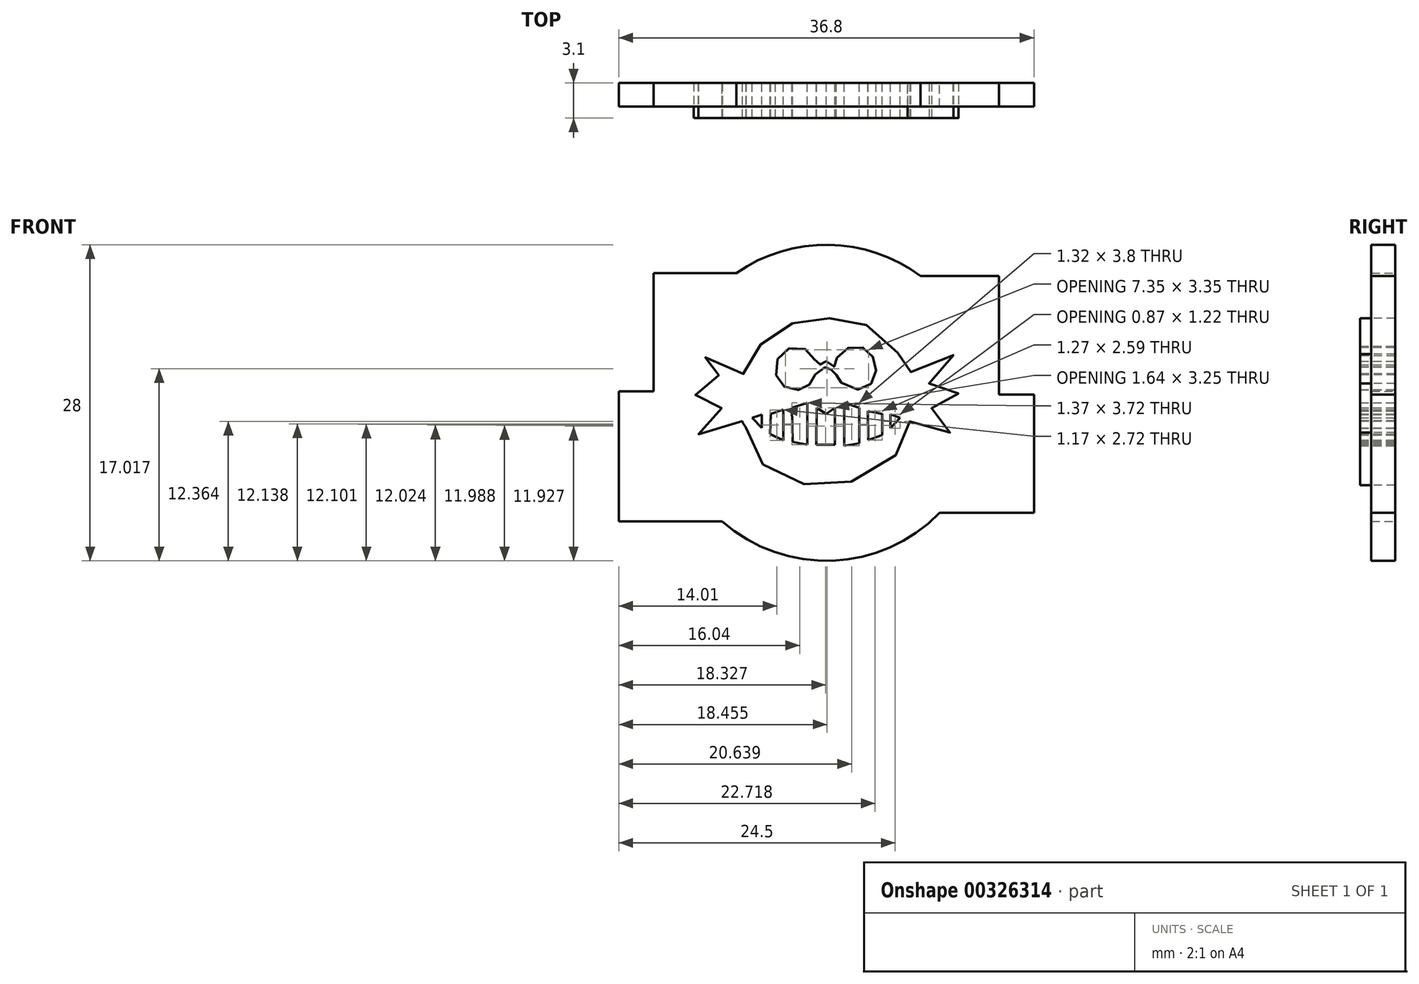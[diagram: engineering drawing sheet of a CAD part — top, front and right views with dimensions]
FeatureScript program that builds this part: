
annotation { "Feature Type Name" : "Feature", "Feature Type Description" : "" }
export const myFeature = defineFeature(function(context is Context, id is Id, definition is map)
    precondition{}
    {
        {
            var Q0;
            Q0=qCreatedBy(makeId("Front.planeOp"),FACE);
            var sketch = newSketch(context, id + "F0", { "sketchPlane" : qUnion([Q0])});
            skArc(sketch, "E0", {"start": v(-9.26, -10.5) * mm, "mid": v(-4.95, -13.1) * mm, "end": v(0, -14) * mm});
            skLineSegment(sketch, "E1", {"start": v(0, 0) * mm, "end": v(0, -32.67) * mm});
            skLineSegment(sketch, "E2", {"start": v(0, -32.67) * mm, "end": v(0, 0) * mm});
            skLineSegment(sketch, "E3", {"start": v(0, 0) * mm, "end": v(0, 29.65) * mm});
            skLineSegment(sketch, "E4", {"start": v(0, 29.65) * mm, "end": v(0, 0) * mm});
            skLineSegment(sketch, "E5", {"start": v(-26.07, 0) * mm, "end": v(57.02, 0) * mm});
            skLineSegment(sketch, "E6", {"start": v(-18.4, 1) * mm, "end": v(-15.3, 1) * mm});
            skLineSegment(sketch, "E7", {"start": v(-15.3, 1) * mm, "end": v(-15.3, 11.5) * mm});
            skLineSegment(sketch, "E8", {"start": v(-15.3, 11.5) * mm, "end": v(-7.97, 11.5) * mm});
            skLineSegment(sketch, "E9", {"start": v(-18.4, -10.5) * mm, "end": v(-9.26, -10.5) * mm});
            skPoint(sketch, "E10.start.orphan", {"position": v(-26.07, 0) * mm});
            skLineSegment(sketch, "E11", {"start": v(-18.4, 1) * mm, "end": v(-18.4, -10.5) * mm});
            skArc(sketch, "E12.trimOffspring", {"start": v(0, 14) * mm, "mid": v(-4.18, 13.36) * mm, "end": v(-7.97, 11.5) * mm});
            skSolve(sketch);
        }
        {
            var Q0;
            Q0=qCreatedBy(makeId("Front.planeOp"),FACE);
            var sketch = newSketch(context, id + "F1", { "sketchPlane" : qUnion([Q0])});
            skLineSegment(sketch, "E13", {"start": v(18.4, -9.75) * mm, "end": v(18.4, 0.75) * mm});
            skLineSegment(sketch, "E14", {"start": v(18.4, 0.75) * mm, "end": v(15.3, 0.75) * mm});
            skLineSegment(sketch, "E15", {"start": v(15.3, 0.75) * mm, "end": v(15.3, 11.25) * mm});
            skLineSegment(sketch, "E16", {"start": v(15.3, 11.25) * mm, "end": v(8.34, 11.25) * mm});
            skLineSegment(sketch, "E17", {"start": v(0, 0) * mm, "end": v(0, 19.78) * mm});
            skLineSegment(sketch, "E18", {"start": v(0, 19.78) * mm, "end": v(0, -13.44) * mm});
            skLineSegment(sketch, "E19", {"start": v(18.4, -9.75) * mm, "end": v(10.04, -9.75) * mm});
            skArc(sketch, "E20", {"start": v(0, -14) * mm, "mid": v(14, 0) * mm, "end": v(0, 14) * mm});
            skLineSegment(sketch, "E21", {"start": v(0, -13.44) * mm, "end": v(0, -17.91) * mm});
            skLineSegment(sketch, "E22", {"start": v(0, 14) * mm, "end": v(0, -13.44) * mm});
            skLineSegment(sketch, "E23", {"start": v(0.9, 13.97) * mm, "end": v(0, 14) * mm});
            skSolve(sketch);
        }
        {
            var Q0;
            {var subQ0=sQuery(id+"F0.wireOp",EDGE,"E9");Q0=makeQuery(id+"F0.imprint","IMPRINT",FACE,{"disambiguationData":[TD([[makeQuery(id+"F0.imprint","IMPRINT",EDGE,{"derivedFrom":subQ0}),1.0]])]});}
            var Q1;
            {var subQ0=sQuery(id+"F0.wireOp",EDGE,"E6");Q1=makeQuery(id+"F0.imprint","IMPRINT",FACE,{"disambiguationData":[TD([[makeQuery(id+"F0.imprint","IMPRINT",EDGE,{"derivedFrom":subQ0}),-1.0]])]});}
            var Q2;
            Q2 = qSketchRegion(id + "F1", true);
            extrude(context, id + "F2", {"entities" : qUnion([Q0, Q1, Q2]), "depth" : 2.1 * mm});
        }
        {
            var Q0;
            Q0 = qSketchRegion(id + "F1", true);
            extrude(context, id + "F3", {"entities" : qUnion([Q0]), "operationType" : NewBodyOperationType.ADD, "depth" : 2.1 * mm});
        }
        {
            var Q0;
            Q0=qCreatedBy(makeId("Front.planeOp"),FACE);
            var sketch = newSketch(context, id + "F4", { "sketchPlane" : qUnion([Q0])});
            skFitSpline(sketch, "E24", {"points": [v(-7.22, 2.65) * mm, v(-5.66, 5.36) * mm, v(-2.98, 7.05) * mm, v(0, 7.5) * mm, v(3.02, 7.05) * mm, v(5.86, 5.16) * mm, v(7.22, 2.48) * mm, v(7.26, 2.57) * mm, v(11.25, 4.25) * mm, v(9.11, 1.78) * mm, v(9.52, 1.7) * mm, v(11.7, 0.72) * mm, v(9.32, -0.31) * mm, v(11.21, -2.62) * mm, v(7.47, -1.59) * mm, v(7.46, -1.92) * mm, v(5.25, -5.57) * mm, v(0, -7.28) * mm, v(-4.15, -6.5) * mm, v(-7.1, -3.12) * mm, v(-7.45, -1.6) * mm, v(-11.37, -2.77) * mm, v(-9.28, -0.48) * mm, v(-11.76, 0.6) * mm, v(-9.24, 1.65) * mm, v(-11.33, 4.14) * mm, v(-7.92, 2.78) * mm, v(-7.22, 2.65) * mm]});
            skFitSpline(sketch, "E25", {"points": [v(-1, 2.5) * mm, v(-1.63, 1.46) * mm, v(-3.3, 1.23) * mm, v(-4.5, 2.62) * mm, v(-3.57, 4.72) * mm, v(-1.43, 4.45) * mm, v(-0.77, 3.4) * mm, v(-0.34, 3.52) * mm, v(0, 3.67) * mm, v(0.7, 3.2) * mm, v(1.01, 4.14) * mm, v(2.88, 5) * mm, v(4.2, 3.94) * mm, v(4.24, 2.12) * mm, v(2.65, 1.19) * mm, v(0.82, 2.35) * mm, v(0.9, 2.55) * mm, v(0.28, 3.05) * mm, v(0, 3.17) * mm, v(-1, 2.5) * mm]});
            skFitSpline(sketch, "E26", {"points": [v(-7.08, -1.6) * mm, v(-7.45, -1.6) * mm, v(-2.6, -6.65) * mm, v(-2.28, -6.24) * mm, v(-1.48, -4.78) * mm, v(0, -4.86) * mm, v(1.38, -4.75) * mm, v(2.4, -6.65) * mm, v(7.14, -1.59) * mm, v(6.96, -1.59) * mm, v(5.25, -3.36) * mm, v(0, -4.43) * mm, v(-4.83, -3.7) * mm, v(-7.08, -1.6) * mm]});
            skLineSegment(sketch, "E27", {"start": v(-6.57, -1.33) * mm, "end": v(-5.74, -1.06) * mm});
            skLineSegment(sketch, "E28", {"start": v(-5.74, -1.06) * mm, "end": v(-5.74, -2.23) * mm});
            skLineSegment(sketch, "E29", {"start": v(-5.74, -2.23) * mm, "end": v(-6.57, -1.33) * mm});
            skLineSegment(sketch, "E30", {"start": v(-4.93, -0.98) * mm, "end": v(-3.8, -0.62) * mm});
            skLineSegment(sketch, "E31", {"start": v(-3.8, -0.62) * mm, "end": v(-3.8, -3.33) * mm});
            skLineSegment(sketch, "E32", {"start": v(-3.8, -3.33) * mm, "end": v(-4.98, -2.77) * mm});
            skLineSegment(sketch, "E33", {"start": v(-4.98, -2.77) * mm, "end": v(-4.93, -0.98) * mm});
            skLineSegment(sketch, "E34", {"start": v(-3.04, -0.45) * mm, "end": v(-1.67, 0) * mm});
            skLineSegment(sketch, "E35", {"start": v(-1.67, 0) * mm, "end": v(-1.67, -3.72) * mm});
            skLineSegment(sketch, "E36", {"start": v(-1.67, -3.72) * mm, "end": v(-3, -3.46) * mm});
            skLineSegment(sketch, "E37", {"start": v(-3, -3.46) * mm, "end": v(-3.04, -0.45) * mm});
            skLineSegment(sketch, "E38", {"start": v(-0.87, -0.45) * mm, "end": v(0, -0.98) * mm});
            skLineSegment(sketch, "E39", {"start": v(0, -0.98) * mm, "end": v(0.75, -0.45) * mm});
            skLineSegment(sketch, "E40", {"start": v(0.75, -0.45) * mm, "end": v(0.75, -3.7) * mm});
            skLineSegment(sketch, "E41", {"start": v(0.75, -3.7) * mm, "end": v(-0.9, -3.7) * mm});
            skLineSegment(sketch, "E42", {"start": v(-0.9, -3.7) * mm, "end": v(-0.87, -0.45) * mm});
            skLineSegment(sketch, "E43", {"start": v(1.58, 0) * mm, "end": v(1.58, -3.8) * mm});
            skLineSegment(sketch, "E44", {"start": v(1.58, -3.8) * mm, "end": v(2.9, -3.58) * mm});
            skLineSegment(sketch, "E45", {"start": v(2.9, -3.58) * mm, "end": v(2.9, -0.45) * mm});
            skLineSegment(sketch, "E46", {"start": v(2.9, -0.45) * mm, "end": v(1.58, 0) * mm});
            skLineSegment(sketch, "E47", {"start": v(3.68, -0.72) * mm, "end": v(4.95, -0.98) * mm});
            skLineSegment(sketch, "E48", {"start": v(4.95, -0.98) * mm, "end": v(4.95, -2.84) * mm});
            skLineSegment(sketch, "E49", {"start": v(4.95, -2.84) * mm, "end": v(3.7, -3.3) * mm});
            skLineSegment(sketch, "E50", {"start": v(3.7, -3.3) * mm, "end": v(3.68, -0.72) * mm});
            skPoint(sketch, "E51.end.orphan", {"position": v(5.66, -1.33) * mm});
            skLineSegment(sketch, "E52", {"start": v(5.66, -1.02) * mm, "end": v(6.54, -1.33) * mm});
            skLineSegment(sketch, "E53", {"start": v(6.54, -1.33) * mm, "end": v(5.66, -2.25) * mm});
            skLineSegment(sketch, "E54", {"start": v(5.66, -2.25) * mm, "end": v(5.66, -1.02) * mm});
            skSolve(sketch);
        }
        {
            var Q0;
            Q0 = qSketchRegion(id + "F4", true);
            extrude(context, id + "F5", {"entities" : qUnion([Q0]), "depth" : 3.1 * mm});
        }
        {
            var Q0;
            Q0=makeQuery(id+"F2.opExtrude","SWEPT_BODY",BODY,{"disambiguationData":[OSD([sQuery(id+"F0.wireOp",EDGE,"E0"),sQuery(id+"F0.wireOp",EDGE,"E2"),sQuery(id+"F0.wireOp",EDGE,"E4"),sQuery(id+"F0.wireOp",EDGE,"E6"),sQuery(id+"F0.wireOp",EDGE,"E7"),sQuery(id+"F0.wireOp",EDGE,"E8"),sQuery(id+"F0.wireOp",EDGE,"E9"),sQuery(id+"F0.wireOp",EDGE,"E11"),sQuery(id+"F0.wireOp",EDGE,"E12.trimOffspring")])]});
            transform(context, id + "F6", {"entities" : qUnion([Q0]), "transformType" : TransformType.TRANSLATION_3D, "dx" : 0 * mm, "dy" : 0 * mm, "dz" : 0 * mm, "makeCopy" : true});
        }
    });
